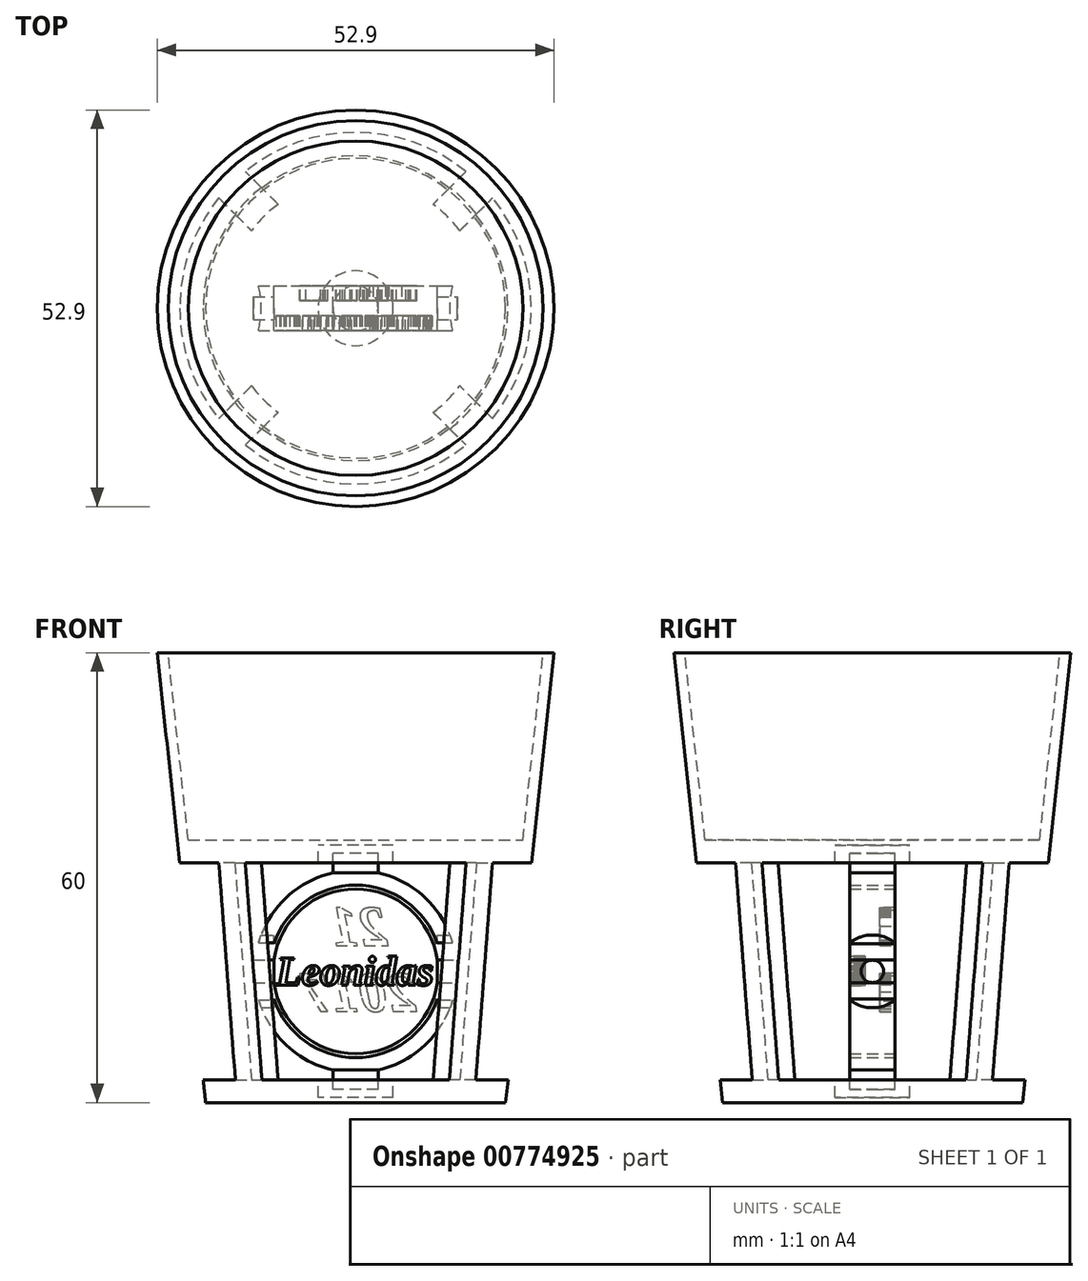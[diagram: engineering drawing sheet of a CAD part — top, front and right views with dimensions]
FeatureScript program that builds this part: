
annotation { "Feature Type Name" : "Feature", "Feature Type Description" : "" }
export const myFeature = defineFeature(function(context is Context, id is Id, definition is map)
    precondition{}
    {
        {
            var Q0;
            Q0=qCreatedBy(makeId("Front.planeOp"),FACE);
            var sketch = newSketch(context, id + "F0", { "sketchPlane" : qUnion([Q0])});
            skLineSegment(sketch, "E0", {"start": v(0, 0) * mm, "end": v(20, 0) * mm});
            skLineSegment(sketch, "E1", {"start": v(20, 0) * mm, "end": v(26.45, 60) * mm});
            skLineSegment(sketch, "E2", {"start": v(26.45, 60) * mm, "end": v(25, 60) * mm});
            skLineSegment(sketch, "E3", {"start": v(25, 60) * mm, "end": v(22.31, 35) * mm});
            skLineSegment(sketch, "E4", {"start": v(22.31, 35) * mm, "end": v(0, 35) * mm});
            skLineSegment(sketch, "E5", {"start": v(17.3, 3) * mm, "end": v(20.42, 32) * mm});
            skLineSegment(sketch, "E6", {"start": v(20.42, 32) * mm, "end": v(0, 32) * mm});
            skLineSegment(sketch, "E7", {"start": v(17.3, 3) * mm, "end": v(0, 3) * mm});
            skLineSegment(sketch, "E8.trimOffspring", {"start": v(0, 3) * mm, "end": v(0, 0) * mm});
            skLineSegment(sketch, "E9", {"start": v(0, 32) * mm, "end": v(0, 35) * mm});
            skSolve(sketch);
        }
        {
            var Q0;
            Q0=qSketchRegion(id+"F0",true);
            var Q1;
            Q1=sQuery(id+"F0.wireOp",EDGE,"E9");
            revolve(context, id + "F1", {"surfaceOperationType" : NewSurfaceOperationType.NEW, "entities" : qUnion([Q0]), "axis" : qUnion([Q1]), "revolveType" : RevolveType.FULL});
        }
        {
            var Q0;
            Q0=makeQuery(id+"F1.opRevolve","SWEPT_FACE",FACE,{"disambiguationData":[OSD([sQuery(id+"F0.wireOp",EDGE,"E7")])]});
            var sketch = newSketch(context, id + "F2", { "sketchPlane" : qUnion([Q0])});
            skArc(sketch, "E10", {"start": v(15.68, 19.22) * mm, "mid": v(0, 24.8) * mm, "end": v(-15.68, 19.22) * mm});
            skLineSegment(sketch, "E11", {"start": v(0, 0) * mm, "end": v(0, 28.4) * mm, "construction": true});
            skLineSegment(sketch, "E12", {"start": v(0, 0) * mm, "end": v(28.58, 0) * mm, "construction": true});
            skLineSegment(sketch, "E13", {"start": v(0, 0) * mm, "end": v(20.34, 20.34) * mm, "construction": true});
            skLineSegment(sketch, "E14", {"start": v(15.8, 12.26) * mm, "end": v(19.22, 15.68) * mm});
            skLineSegment(sketch, "E15.MirrorCS", {"start": v(12.26, 15.8) * mm, "end": v(15.68, 19.22) * mm});
            skLineSegment(sketch, "E16.MirrorCS", {"start": v(-15.8, 12.26) * mm, "end": v(-19.22, 15.68) * mm});
            skLineSegment(sketch, "E17.MirrorCS", {"start": v(-12.26, 15.8) * mm, "end": v(-15.68, 19.22) * mm});
            skLineSegment(sketch, "E18.MirrorCS", {"start": v(12.26, -15.8) * mm, "end": v(15.68, -19.22) * mm});
            skLineSegment(sketch, "E19.MirrorCS", {"start": v(-12.26, -15.8) * mm, "end": v(-15.68, -19.22) * mm});
            skLineSegment(sketch, "E20.MirrorCS", {"start": v(15.8, -12.26) * mm, "end": v(19.22, -15.68) * mm});
            skLineSegment(sketch, "E21.MirrorCS", {"start": v(-15.8, -12.26) * mm, "end": v(-19.22, -15.68) * mm});
            skPoint(sketch, "E22.end.orphan", {"position": v(19.93, 19.93) * mm});
            skPoint(sketch, "E22.start.orphan", {"position": v(21.7, 18.16) * mm});
            skPoint(sketch, "E23.MirrorCS.start.orphan", {"position": v(18.16, 21.7) * mm});
            skPoint(sketch, "E24.orphan", {"position": v(-18.16, 21.7) * mm});
            skPoint(sketch, "E25.MirrorCS.end.orphan", {"position": v(-19.93, 19.93) * mm});
            skPoint(sketch, "E26.MirrorCS.start.orphan", {"position": v(-21.7, 18.16) * mm});
            skArc(sketch, "E27.trimOffspring", {"start": v(-19.22, 15.68) * mm, "mid": v(-24.8, 0) * mm, "end": v(-19.22, -15.68) * mm});
            skPoint(sketch, "E28.orphan", {"position": v(-18.16, -21.7) * mm});
            skPoint(sketch, "E29.MirrorCS.end.orphan", {"position": v(-19.93, -19.93) * mm});
            skPoint(sketch, "E30.MirrorCS.start.orphan", {"position": v(-21.7, -18.16) * mm});
            skArc(sketch, "E31.trimOffspring", {"start": v(-15.68, -19.22) * mm, "mid": v(0, -24.8) * mm, "end": v(15.68, -19.22) * mm});
            skPoint(sketch, "E32.MirrorCS.end.orphan", {"position": v(19.93, -19.93) * mm});
            skPoint(sketch, "E32.MirrorCS.start.orphan", {"position": v(21.7, -18.16) * mm});
            skPoint(sketch, "E33.MirrorCS.start.orphan", {"position": v(18.16, -21.7) * mm});
            skArc(sketch, "E34.trimOffspring", {"start": v(19.22, -15.68) * mm, "mid": v(24.8, 0) * mm, "end": v(19.22, 15.68) * mm});
            skArc(sketch, "E35", {"start": v(-12.23, 8.7) * mm, "mid": v(-15, 0) * mm, "end": v(-12.23, -8.7) * mm});
            skLineSegment(sketch, "E36", {"start": v(-12.26, -15.8) * mm, "end": v(-8.7, -12.23) * mm});
            skLineSegment(sketch, "E37", {"start": v(-15.8, -12.26) * mm, "end": v(-12.23, -8.7) * mm});
            skLineSegment(sketch, "E38", {"start": v(12.26, -15.8) * mm, "end": v(8.7, -12.23) * mm});
            skLineSegment(sketch, "E39", {"start": v(15.8, -12.26) * mm, "end": v(12.23, -8.7) * mm});
            skLineSegment(sketch, "E40", {"start": v(15.8, 12.26) * mm, "end": v(12.23, 8.7) * mm});
            skLineSegment(sketch, "E41", {"start": v(12.26, 15.8) * mm, "end": v(8.7, 12.23) * mm});
            skLineSegment(sketch, "E42", {"start": v(-12.26, 15.8) * mm, "end": v(-8.7, 12.23) * mm});
            skLineSegment(sketch, "E43", {"start": v(-15.8, 12.26) * mm, "end": v(-12.23, 8.7) * mm});
            skArc(sketch, "E44.trimOffspring", {"start": v(8.7, 12.23) * mm, "mid": v(0, 15) * mm, "end": v(-8.7, 12.23) * mm});
            skArc(sketch, "E45.trimOffspring", {"start": v(12.23, -8.7) * mm, "mid": v(15, 0) * mm, "end": v(12.23, 8.7) * mm});
            skArc(sketch, "E46.trimOffspring", {"start": v(-8.7, -12.23) * mm, "mid": v(0, -15) * mm, "end": v(8.7, -12.23) * mm});
            skSolve(sketch);
        }
        {
            var Q0;
            Q0=qSketchRegion(id+"F2",true);
            extrude(context, id + "F3", {"entities" : qUnion([Q0]), "operationType" : NewBodyOperationType.REMOVE, "depth" : 29 * mm, "offsetDistance" : 25 * mm});
        }
        {
            var Q0;
            Q0=makeQuery(id+"F3.boolean.opBoolean","MERGE",FACE,{"derivedFrom":[makeQuery(id+"F1.opRevolve","SWEPT_FACE",FACE,{"disambiguationData":[OSD([sQuery(id+"F0.wireOp",EDGE,"E7")])]}),makeQuery(id+"F3.opExtrude","CAP_FACE",FACE,{"disambiguationData":[OSD([sQuery(id+"F2.wireOp",EDGE,"E10"),sQuery(id+"F2.wireOp",EDGE,"E15.MirrorCS"),sQuery(id+"F2.wireOp",EDGE,"E17.MirrorCS"),sQuery(id+"F2.wireOp",EDGE,"E41"),sQuery(id+"F2.wireOp",EDGE,"E42"),sQuery(id+"F2.wireOp",EDGE,"E44.trimOffspring")])],"isStart":true}),makeQuery(id+"F3.opExtrude","CAP_FACE",FACE,{"disambiguationData":[OSD([sQuery(id+"F2.wireOp",EDGE,"E14"),sQuery(id+"F2.wireOp",EDGE,"E20.MirrorCS"),sQuery(id+"F2.wireOp",EDGE,"E34.trimOffspring"),sQuery(id+"F2.wireOp",EDGE,"E39"),sQuery(id+"F2.wireOp",EDGE,"E40"),sQuery(id+"F2.wireOp",EDGE,"E45.trimOffspring")])],"isStart":true}),makeQuery(id+"F3.opExtrude","CAP_FACE",FACE,{"disambiguationData":[OSD([sQuery(id+"F2.wireOp",EDGE,"E16.MirrorCS"),sQuery(id+"F2.wireOp",EDGE,"E21.MirrorCS"),sQuery(id+"F2.wireOp",EDGE,"E27.trimOffspring"),sQuery(id+"F2.wireOp",EDGE,"E35"),sQuery(id+"F2.wireOp",EDGE,"E37"),sQuery(id+"F2.wireOp",EDGE,"E43")])],"isStart":true}),makeQuery(id+"F3.opExtrude","CAP_FACE",FACE,{"disambiguationData":[OSD([sQuery(id+"F2.wireOp",EDGE,"E18.MirrorCS"),sQuery(id+"F2.wireOp",EDGE,"E19.MirrorCS"),sQuery(id+"F2.wireOp",EDGE,"E31.trimOffspring"),sQuery(id+"F2.wireOp",EDGE,"E36"),sQuery(id+"F2.wireOp",EDGE,"E38"),sQuery(id+"F2.wireOp",EDGE,"E46.trimOffspring")])],"isStart":true})]});
            var sketch = newSketch(context, id + "F4", { "sketchPlane" : qUnion([Q0])});
            skCircle(sketch, "E47", {"center": v(0, 0) * mm, "radius": 3.5 * mm});
            skSolve(sketch);
        }
        {
            var Q0;
            Q0=qSketchRegion(id+"F4",true);
            extrude(context, id + "F5", {"entities" : qUnion([Q0]), "operationType" : NewBodyOperationType.REMOVE, "oppositeDirection" : true, "depth" : 2 * mm, "offsetDistance" : 25 * mm, "hasSecondDirection" : true, "secondDirectionOppositeDirection" : false, "secondDirectionDepth" : 31 * mm});
        }
        {
            var Q0;
            Q0=qCreatedBy(makeId("Front.planeOp"),FACE);
            var sketch = newSketch(context, id + "F6", { "sketchPlane" : qUnion([Q0])});
            skLineSegment(sketch, "E48", {"start": v(0, 33.25) * mm, "end": v(3, 33.25) * mm});
            skLineSegment(sketch, "E49", {"start": v(3, 33.25) * mm, "end": v(3, 30.66) * mm});
            skLineSegment(sketch, "E50", {"start": v(3, 30.66) * mm, "end": v(3, 30.66) * mm});
            skArc(sketch, "E51", {"start": v(3, 4.34) * mm, "mid": v(13.5, 17.5) * mm, "end": v(3, 30.66) * mm});
            skLineSegment(sketch, "E52", {"start": v(3, 4.34) * mm, "end": v(3, 1.75) * mm});
            skLineSegment(sketch, "E53", {"start": v(3, 1.75) * mm, "end": v(0, 1.75) * mm});
            skLineSegment(sketch, "E54.MirrorCS", {"start": v(0, 33.25) * mm, "end": v(-3, 33.25) * mm});
            skLineSegment(sketch, "E55.MirrorCS", {"start": v(-3, 33.25) * mm, "end": v(-3, 30.66) * mm});
            skLineSegment(sketch, "E56.MirrorCS", {"start": v(-3, 1.75) * mm, "end": v(0, 1.75) * mm});
            skLineSegment(sketch, "E57.MirrorCS", {"start": v(-3, 4.34) * mm, "end": v(-3, 1.75) * mm});
            skArc(sketch, "E58.MirrorCS", {"start": v(-3, 4.34) * mm, "mid": v(-13.5, 17.5) * mm, "end": v(-3, 30.66) * mm});
            skCircle(sketch, "E59", {"center": v(0, 17.5) * mm, "radius": 11.5 * mm});
            skSolve(sketch);
        }
        {
            var Q0;
            Q0 = qSketchRegion(id + "F6", true);
            extrude(context, id + "F7", {"entities" : qUnion([Q0]), "endBound" : BoundingType.SYMMETRIC, "depth" : 6 * mm, "offsetDistance" : 25 * mm});
        }
        {
            var Q0;
            Q0=qCreatedBy(makeId("Right.planeOp"),FACE);
            var sketch = newSketch(context, id + "F8", { "sketchPlane" : qUnion([Q0])});
            skCircle(sketch, "E60", {"center": v(0, 17.5) * mm, "radius": 2 * mm});
            skSolve(sketch);
        }
        {
            var Q0;
            Q0 = qSketchRegion(id + "F8", true);
            extrude(context, id + "F9", {"entities" : qUnion([Q0]), "operationType" : NewBodyOperationType.REMOVE, "endBound" : BoundingType.SYMMETRIC, "depth" : 30 * mm, "offsetDistance" : 25 * mm});
        }
        {
            var Q0;
            Q0=qCreatedBy(makeId("Front.planeOp"),FACE);
            var sketch = newSketch(context, id + "F10", { "sketchPlane" : qUnion([Q0])});
            skArc(sketch, "E61", {"start": v(10.9, 19) * mm, "mid": v(0, 28.5) * mm, "end": v(-10.9, 19) * mm});
            skLineSegment(sketch, "E62", {"start": v(-13.8, 17.5) * mm, "end": v(14.42, 17.5) * mm, "construction": true});
            skLineSegment(sketch, "E63", {"start": v(10.9, 16) * mm, "end": v(13.59, 16) * mm});
            skLineSegment(sketch, "E64", {"start": v(13.59, 16) * mm, "end": v(13.59, 17.5) * mm});
            skLineSegment(sketch, "E65.MirrorCS", {"start": v(10.9, 19) * mm, "end": v(13.59, 19) * mm});
            skLineSegment(sketch, "E66.MirrorCS", {"start": v(13.59, 19) * mm, "end": v(13.59, 17.5) * mm});
            skLineSegment(sketch, "E67.MirrorCS", {"start": v(-10.9, 16) * mm, "end": v(-13.59, 16) * mm});
            skLineSegment(sketch, "E68.MirrorCS", {"start": v(-13.59, 19) * mm, "end": v(-13.59, 17.5) * mm});
            skLineSegment(sketch, "E69.MirrorCS", {"start": v(-13.59, 16) * mm, "end": v(-13.59, 17.5) * mm});
            skLineSegment(sketch, "E70.MirrorCS", {"start": v(-10.9, 19) * mm, "end": v(-13.59, 19) * mm});
            skArc(sketch, "E71.trimOffspring", {"start": v(-10.9, 16) * mm, "mid": v(0, 6.5) * mm, "end": v(10.9, 16) * mm});
            skSolve(sketch);
        }
        {
            var Q0;
            Q0 = qSketchRegion(id + "F10", true);
            extrude(context, id + "F11", {"entities" : qUnion([Q0]), "endBound" : BoundingType.SYMMETRIC, "depth" : 6 * mm, "offsetDistance" : 25 * mm});
        }
        {
            var Q0;
            Q0=qCreatedBy(makeId("Front.planeOp"),FACE);
            var sketch = newSketch(context, id + "F12", { "sketchPlane" : qUnion([Q0])});
            skLineSegment(sketch, "E72.0", {"start": v(3, 33.25) * mm, "end": v(3, 30.66) * mm});
            skLineSegment(sketch, "E73.0", {"start": v(0, 33.25) * mm, "end": v(3, 33.25) * mm});
            skLineSegment(sketch, "E74", {"start": v(0, 33.25) * mm, "end": v(0, 34.3) * mm});
            skLineSegment(sketch, "E75", {"start": v(0, 34.3) * mm, "end": v(5, 34.3) * mm});
            skLineSegment(sketch, "E76", {"start": v(5, 34.3) * mm, "end": v(5, 30.66) * mm});
            skLineSegment(sketch, "E77", {"start": v(5, 30.66) * mm, "end": v(3, 30.66) * mm});
            skLineSegment(sketch, "E78", {"start": v(0, 17.5) * mm, "end": v(16.9, 17.5) * mm, "construction": true});
            skLineSegment(sketch, "E79.MirrorCS", {"start": v(5, 4.34) * mm, "end": v(3, 4.34) * mm});
            skLineSegment(sketch, "E80.MirrorCS", {"start": v(5, 0.7) * mm, "end": v(5, 4.34) * mm});
            skLineSegment(sketch, "E81.MirrorCS", {"start": v(0, 0.7) * mm, "end": v(5, 0.7) * mm});
            skLineSegment(sketch, "E82.MirrorCS", {"start": v(3, 1.75) * mm, "end": v(3, 4.34) * mm});
            skLineSegment(sketch, "E83.MirrorCS", {"start": v(0, 1.75) * mm, "end": v(3, 1.75) * mm});
            skLineSegment(sketch, "E84.MirrorCS", {"start": v(0, 1.75) * mm, "end": v(0, 0.7) * mm});
            skSolve(sketch);
        }
        {
            var Q0;
            Q0 = qSketchRegion(id + "F12", true);
            var Q1;
            Q1=sQuery(id+"F12.wireOp",EDGE,"E74");
            revolve(context, id + "F13", {"operationType" : NewBodyOperationType.REMOVE, "surfaceOperationType" : NewSurfaceOperationType.NEW, "entities" : qUnion([Q0]), "axis" : qUnion([Q1]), "revolveType" : RevolveType.FULL, "oppositeDirection" : true});
        }
        {
            var Q0;
            Q0=qCreatedBy(makeId("Front.planeOp"),FACE);
            var sketch = newSketch(context, id + "F14", { "sketchPlane" : qUnion([Q0])});
            skLineSegment(sketch, "E85.0", {"start": v(10.9, 19) * mm, "end": v(13.59, 19) * mm});
            skLineSegment(sketch, "E86.0", {"start": v(13.59, 17.5) * mm, "end": v(13.59, 19) * mm});
            skLineSegment(sketch, "E87", {"start": v(0, 17.5) * mm, "end": v(17.25, 17.5) * mm, "construction": true});
            skPoint(sketch, "E88.orphan", {"position": v(13.59, 16) * mm});
            skLineSegment(sketch, "E89", {"start": v(10.9, 19) * mm, "end": v(10.9, 22.35) * mm});
            skLineSegment(sketch, "E90", {"start": v(10.9, 22.35) * mm, "end": v(15, 22.35) * mm});
            skLineSegment(sketch, "E91", {"start": v(15, 22.35) * mm, "end": v(15, 17.5) * mm});
            skLineSegment(sketch, "E92", {"start": v(15, 17.5) * mm, "end": v(13.59, 17.5) * mm});
            skLineSegment(sketch, "E93.MirrorCS", {"start": v(-13.59, 17.5) * mm, "end": v(-13.59, 19) * mm});
            skLineSegment(sketch, "E94.MirrorCS", {"start": v(-10.9, 22.35) * mm, "end": v(-15, 22.35) * mm});
            skLineSegment(sketch, "E95.MirrorCS", {"start": v(-10.9, 19) * mm, "end": v(-10.9, 22.35) * mm});
            skLineSegment(sketch, "E96.MirrorCS", {"start": v(-15, 22.35) * mm, "end": v(-15, 17.5) * mm});
            skLineSegment(sketch, "E97.MirrorCS", {"start": v(-15, 17.5) * mm, "end": v(-13.59, 17.5) * mm});
            skLineSegment(sketch, "E98.MirrorCS", {"start": v(-10.9, 19) * mm, "end": v(-13.59, 19) * mm});
            skSolve(sketch);
        }
        {
            var Q0;
            Q0 = qSketchRegion(id + "F14", true);
            var Q1;
            Q1=sQuery(id+"F14.wireOp",EDGE,"E97.MirrorCS");
            revolve(context, id + "F15", {"operationType" : NewBodyOperationType.REMOVE, "surfaceOperationType" : NewSurfaceOperationType.NEW, "entities" : qUnion([Q0]), "axis" : qUnion([Q1]), "revolveType" : RevolveType.FULL, "oppositeDirection" : true});
        }
        {
            var Q0;
            Q0=makeQuery(id+"F11.opExtrude","CAP_FACE",FACE,{"disambiguationData":[OSD([sQuery(id+"F10.wireOp",EDGE,"E61"),sQuery(id+"F10.wireOp",EDGE,"E63"),sQuery(id+"F10.wireOp",EDGE,"E64"),sQuery(id+"F10.wireOp",EDGE,"E65.MirrorCS"),sQuery(id+"F10.wireOp",EDGE,"E66.MirrorCS"),sQuery(id+"F10.wireOp",EDGE,"E67.MirrorCS"),sQuery(id+"F10.wireOp",EDGE,"E68.MirrorCS"),sQuery(id+"F10.wireOp",EDGE,"E69.MirrorCS"),sQuery(id+"F10.wireOp",EDGE,"E70.MirrorCS"),sQuery(id+"F10.wireOp",EDGE,"E71.trimOffspring")])],"isStart":false});
            var sketch = newSketch(context, id + "F16", { "sketchPlane" : qUnion([Q0])});
            skText(sketch, "E99", { "text": "Leonidas", "fontName": "Tinos-BoldItalic.ttf"});
            const initialGuessF16  = {"E99": [-0.0106, 0.01566, 1, 0, 0.004]};
            skSetInitialGuess(sketch, initialGuessF16);
            skSolve(sketch);
        }
        {
            var Q0;
            Q0 = qSketchRegion(id + "F16", true);
            extrude(context, id + "F17", {"entities" : qUnion([Q0]), "operationType" : NewBodyOperationType.REMOVE, "oppositeDirection" : true, "depth" : 2 * mm, "offsetDistance" : 25 * mm});
        }
        {
            var Q0;
            Q0=makeQuery(id+"F11.opExtrude","CAP_FACE",FACE,{"disambiguationData":[OSD([sQuery(id+"F10.wireOp",EDGE,"E61"),sQuery(id+"F10.wireOp",EDGE,"E63"),sQuery(id+"F10.wireOp",EDGE,"E64"),sQuery(id+"F10.wireOp",EDGE,"E65.MirrorCS"),sQuery(id+"F10.wireOp",EDGE,"E66.MirrorCS"),sQuery(id+"F10.wireOp",EDGE,"E67.MirrorCS"),sQuery(id+"F10.wireOp",EDGE,"E68.MirrorCS"),sQuery(id+"F10.wireOp",EDGE,"E69.MirrorCS"),sQuery(id+"F10.wireOp",EDGE,"E70.MirrorCS"),sQuery(id+"F10.wireOp",EDGE,"E71.trimOffspring")])],"isStart":true});
            var sketch = newSketch(context, id + "F18", { "sketchPlane" : qUnion([Q0])});
            skText(sketch, "E100", { "text": "  21\n2017", "fontName": "Tinos-BoldItalic.ttf"});
            const initialGuessF18  = {"E100": [-0.00805, 0.02095, 1, 0, 0.0055]};
            skSetInitialGuess(sketch, initialGuessF18);
            skSolve(sketch);
        }
        {
            var Q0;
            Q0 = qSketchRegion(id + "F18", true);
            extrude(context, id + "F19", {"entities" : qUnion([Q0]), "operationType" : NewBodyOperationType.REMOVE, "oppositeDirection" : true, "depth" : 2 * mm, "offsetDistance" : 25 * mm});
        }
    });
